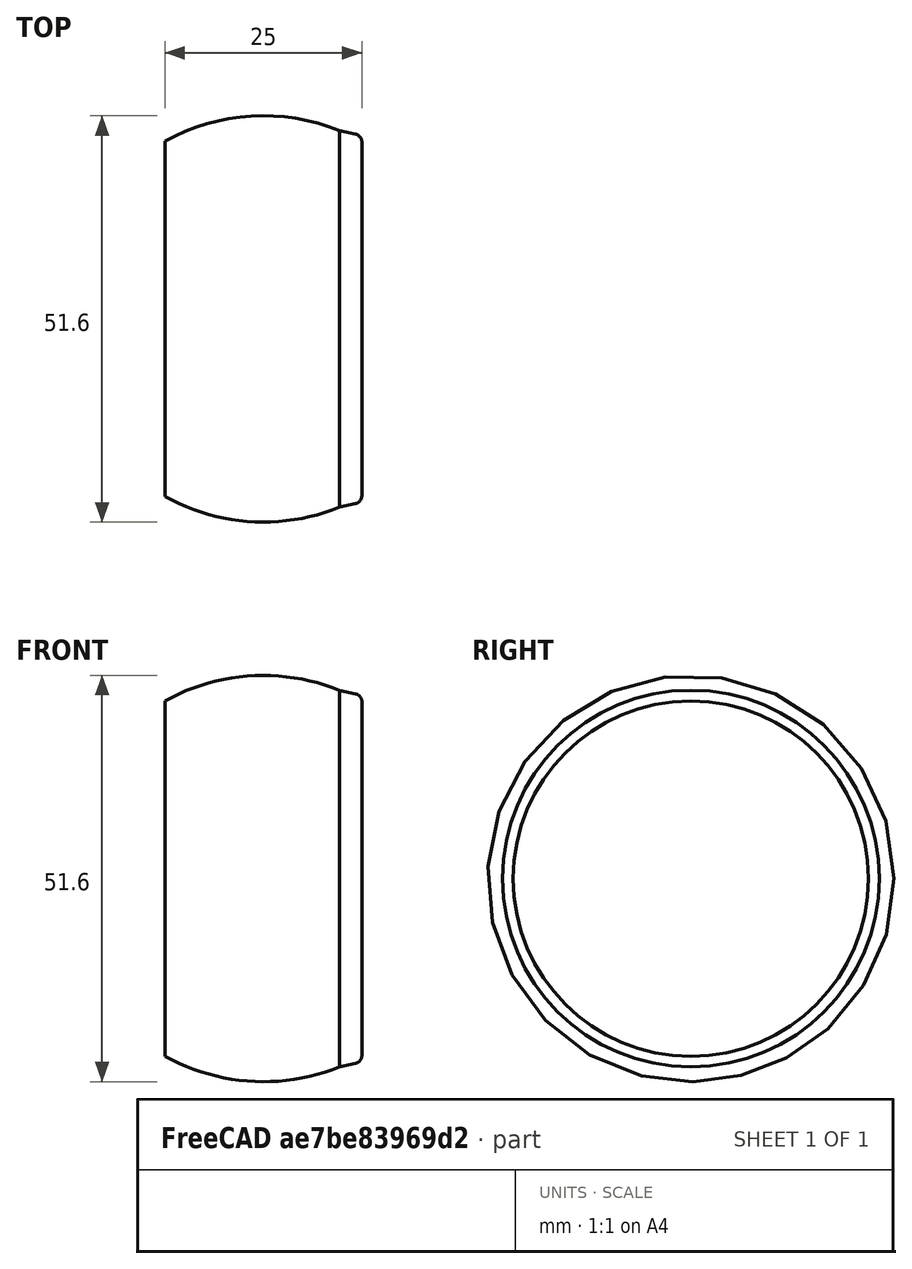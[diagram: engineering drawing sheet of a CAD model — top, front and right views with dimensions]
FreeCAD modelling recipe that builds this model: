
FCSTD DOCUMENT  (FreeCAD 0.18R16110 (Git))
Label: hubcut
License: All rights reserved
LicenseURL: http://en.wikipedia.org/wiki/All_rights_reserved
objects: Sketcher::SketchObject×1, Mesh::Feature×1, Part::Revolution×1, Part::Fillet×1
note: 3 computed .brp shape members not serialized (recipe doc carries the construction recipe); baked Part::Feature solids carry a one-line shape summary decoded from their .brp

FEATURE [Sketcher::SketchObject] Sketch
  sketch-geometry (8):
    g0: ArcOfCircle CenterX=0 CenterY=0.00162187 CenterZ=0 NormalX=0 NormalY=0 NormalZ=1 AngleXU=0 Radius=25.8 StartAngle=1.18729 EndAngle=2.07671
    g1: LineSegment StartX=12.5029 StartY=21.8997 StartZ=0 EndX=12.5029 EndY=19.8997 EndZ=0
    g2: LineSegment StartX=-12.5029 StartY=22.5697 StartZ=0 EndX=-12.5029 EndY=19.8997 EndZ=0
    g3: LineSegment StartX=9.6537 StartY=23.9275 StartZ=0 EndX=12.5029 EndY=23.2897 EndZ=0
    g4: LineSegment StartX=12.5029 StartY=23.2897 StartZ=0 EndX=12.5029 EndY=21.8997 EndZ=0
    g5: LineSegment StartX=-12.5029 StartY=19.8997 StartZ=0 EndX=-12.5029 EndY=0 EndZ=0
    g6: LineSegment StartX=12.5029 StartY=19.8997 StartZ=0 EndX=12.5029 EndY=0 EndZ=0
    g7: LineSegment StartX=-12.5029 StartY=0 StartZ=0 EndX=12.5029 EndY=0 EndZ=0
  constraints (19):
    c: Vertical(g1)
    c: Coincident(g2,g0)
    c: Vertical(g2)
    c: Symmetric(g1,g2,g-2)
    c: Coincident(g3,g4)
    c: Coincident(g4,g1)
    c: Coincident(g0,g3)
    c: Vertical(g4)
    c: Radius(g0) = 25.8
    c: DistanceY(g4,g4) = 1.39
    c: DistanceY(g1,g1) = 2
    c: Coincident(g5,g2)
    c: PointOnObject(g5,g-1)
    c: Vertical(g5)
    c: Coincident(g6,g1)
    c: PointOnObject(g6,g-1)
    c: Vertical(g6)
    c: Coincident(g7,g5)
    c: Coincident(g7,g6)
FEATURE [Mesh::Feature] leg
  Placement = pos=(19.76,-21,0) rot=(0,1,0;-1.5708rad)
FEATURE [Part::Revolution] Revolve
  Angle = 360
  Axis = (1,0,0)
  Base = (0,0,0)
  FaceMakerClass = Part::FaceMakerBullseye
  Solid = false
  Source = -> Sketch
  Symmetric = false
FEATURE [Part::Fillet] Fillet
  Base = -> Revolve
  Edges = 1 edges r=1: [Edge2]
